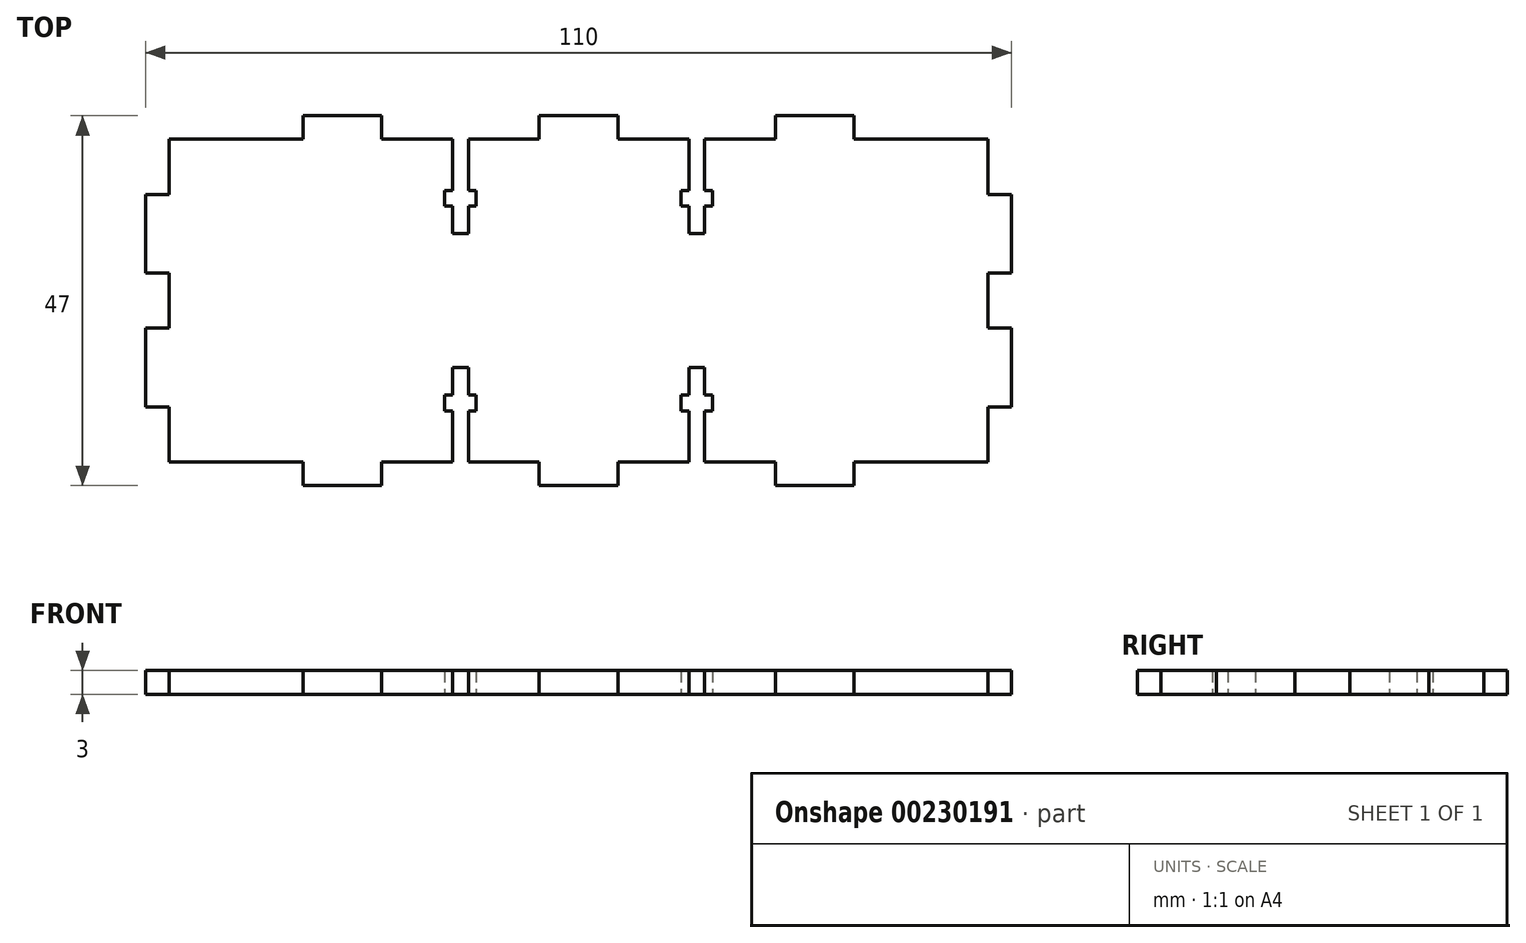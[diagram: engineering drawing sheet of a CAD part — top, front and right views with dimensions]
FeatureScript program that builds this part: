
annotation { "Feature Type Name" : "Feature", "Feature Type Description" : "" }
export const myFeature = defineFeature(function(context is Context, id is Id, definition is map)
    precondition{}
    {
        {
            var Q0;
            Q0=qCreatedBy(makeId("Top.planeOp"),FACE);
            var sketch = newSketch(context, id + "F0", { "sketchPlane" : qUnion([Q0])});
            skLineSegment(sketch, "E0", {"start": v(0, 0) * mm, "end": v(0, 7) * mm});
            skLineSegment(sketch, "E1", {"start": v(0, 7) * mm, "end": v(3, 7) * mm});
            skLineSegment(sketch, "E2", {"start": v(3, 7) * mm, "end": v(3, 17) * mm});
            skLineSegment(sketch, "E3", {"start": v(3, 17) * mm, "end": v(0, 17) * mm});
            skLineSegment(sketch, "E4", {"start": v(0, 17) * mm, "end": v(0, 24) * mm});
            skLineSegment(sketch, "E5", {"start": v(0, 24) * mm, "end": v(3, 24) * mm});
            skLineSegment(sketch, "E6", {"start": v(3, 24) * mm, "end": v(3, 34) * mm});
            skLineSegment(sketch, "E7", {"start": v(3, 34) * mm, "end": v(0, 34) * mm});
            skLineSegment(sketch, "E8", {"start": v(0, 34) * mm, "end": v(0, 41) * mm});
            skLineSegment(sketch, "E9", {"start": v(0, 41) * mm, "end": v(-17, 41) * mm});
            skLineSegment(sketch, "E10", {"start": v(-17, 41) * mm, "end": v(-17, 44) * mm});
            skLineSegment(sketch, "E11", {"start": v(-17, 44) * mm, "end": v(-27, 44) * mm});
            skLineSegment(sketch, "E12", {"start": v(-27, 44) * mm, "end": v(-27, 41) * mm});
            skLineSegment(sketch, "E13", {"start": v(-27, 41) * mm, "end": v(-36, 41) * mm});
            skLineSegment(sketch, "E14", {"start": v(-36, 41) * mm, "end": v(-36, 34.5) * mm});
            skLineSegment(sketch, "E15", {"start": v(-36, 34.5) * mm, "end": v(-35, 34.5) * mm});
            skLineSegment(sketch, "E16", {"start": v(-35, 34.5) * mm, "end": v(-35, 32.5) * mm});
            skLineSegment(sketch, "E17", {"start": v(-35, 32.5) * mm, "end": v(-36, 32.5) * mm});
            skLineSegment(sketch, "E18", {"start": v(-36, 32.5) * mm, "end": v(-36, 29) * mm});
            skLineSegment(sketch, "E19", {"start": v(-36, 29) * mm, "end": v(-38, 29) * mm});
            skLineSegment(sketch, "E20", {"start": v(-38, 29) * mm, "end": v(-38, 32.5) * mm});
            skLineSegment(sketch, "E21", {"start": v(-38, 32.5) * mm, "end": v(-39, 32.5) * mm});
            skLineSegment(sketch, "E22", {"start": v(-39, 32.5) * mm, "end": v(-39, 34.5) * mm});
            skLineSegment(sketch, "E23", {"start": v(-39, 34.5) * mm, "end": v(-38, 34.5) * mm});
            skLineSegment(sketch, "E24", {"start": v(-38, 34.5) * mm, "end": v(-38, 41) * mm});
            skLineSegment(sketch, "E25", {"start": v(-38, 41) * mm, "end": v(-47, 41) * mm});
            skLineSegment(sketch, "E26", {"start": v(-47, 41) * mm, "end": v(-47, 44) * mm});
            skLineSegment(sketch, "E27", {"start": v(-47, 44) * mm, "end": v(-52, 44) * mm});
            skLineSegment(sketch, "E28.MirrorCS", {"start": v(-39, 8.5) * mm, "end": v(-39, 6.5) * mm});
            skLineSegment(sketch, "E29.MirrorCS", {"start": v(-35, 6.5) * mm, "end": v(-35, 8.5) * mm});
            skLineSegment(sketch, "E30.MirrorCS", {"start": v(-38, 8.5) * mm, "end": v(-39, 8.5) * mm});
            skLineSegment(sketch, "E31.MirrorCS", {"start": v(-39, 6.5) * mm, "end": v(-38, 6.5) * mm});
            skLineSegment(sketch, "E32.MirrorCS", {"start": v(-36, 12) * mm, "end": v(-38, 12) * mm});
            skLineSegment(sketch, "E33.MirrorCS", {"start": v(-35, 8.5) * mm, "end": v(-36, 8.5) * mm});
            skLineSegment(sketch, "E34.MirrorCS", {"start": v(-36, 6.5) * mm, "end": v(-35, 6.5) * mm});
            skLineSegment(sketch, "E35.MirrorCS", {"start": v(-36, 8.5) * mm, "end": v(-36, 12) * mm});
            skLineSegment(sketch, "E36.MirrorCS", {"start": v(-38, 12) * mm, "end": v(-38, 8.5) * mm});
            skLineSegment(sketch, "E37.MirrorCS", {"start": v(0, 17) * mm, "end": v(3, 17) * mm});
            skLineSegment(sketch, "E38.MirrorCS", {"start": v(-47, 0) * mm, "end": v(-47, -3) * mm});
            skLineSegment(sketch, "E39.MirrorCS", {"start": v(3, 17) * mm, "end": v(3, 7) * mm});
            skLineSegment(sketch, "E40.MirrorCS", {"start": v(0, 7) * mm, "end": v(0, 0) * mm});
            skLineSegment(sketch, "E41.MirrorCS", {"start": v(3, 7) * mm, "end": v(0, 7) * mm});
            skLineSegment(sketch, "E42.MirrorCS", {"start": v(-38, 0) * mm, "end": v(-47, 0) * mm});
            skLineSegment(sketch, "E43.MirrorCS", {"start": v(-47, -3) * mm, "end": v(-52, -3) * mm});
            skLineSegment(sketch, "E44.MirrorCS", {"start": v(-27, -3) * mm, "end": v(-27, 0) * mm});
            skLineSegment(sketch, "E45.MirrorCS", {"start": v(0, 0) * mm, "end": v(-17, 0) * mm});
            skLineSegment(sketch, "E46.MirrorCS", {"start": v(-38, 6.5) * mm, "end": v(-38, 0) * mm});
            skLineSegment(sketch, "E47.MirrorCS", {"start": v(-27, 0) * mm, "end": v(-36, 0) * mm});
            skLineSegment(sketch, "E48.MirrorCS", {"start": v(-17, 0) * mm, "end": v(-17, -3) * mm});
            skLineSegment(sketch, "E49.MirrorCS", {"start": v(-17, -3) * mm, "end": v(-27, -3) * mm});
            skLineSegment(sketch, "E50.MirrorCS", {"start": v(-36, 0) * mm, "end": v(-36, 6.5) * mm});
            skLineSegment(sketch, "E51.MirrorCS", {"start": v(-107, 7) * mm, "end": v(-104, 7) * mm});
            skLineSegment(sketch, "E52.MirrorCS", {"start": v(-69, 32.5) * mm, "end": v(-68, 32.5) * mm});
            skLineSegment(sketch, "E53.MirrorCS", {"start": v(-104, 7) * mm, "end": v(-107, 7) * mm});
            skLineSegment(sketch, "E54.MirrorCS", {"start": v(-107, 17) * mm, "end": v(-104, 17) * mm});
            skLineSegment(sketch, "E55.MirrorCS", {"start": v(-69, 34.5) * mm, "end": v(-69, 32.5) * mm});
            skLineSegment(sketch, "E56.MirrorCS", {"start": v(-66, 8.5) * mm, "end": v(-65, 8.5) * mm});
            skLineSegment(sketch, "E57.MirrorCS", {"start": v(-104, 17) * mm, "end": v(-107, 17) * mm});
            skLineSegment(sketch, "E58.MirrorCS", {"start": v(-65, 32.5) * mm, "end": v(-65, 34.5) * mm});
            skLineSegment(sketch, "E59.MirrorCS", {"start": v(-69, 6.5) * mm, "end": v(-69, 8.5) * mm});
            skLineSegment(sketch, "E60.MirrorCS", {"start": v(-66, 32.5) * mm, "end": v(-65, 32.5) * mm});
            skLineSegment(sketch, "E61.MirrorCS", {"start": v(-68, 34.5) * mm, "end": v(-69, 34.5) * mm});
            skLineSegment(sketch, "E62.MirrorCS", {"start": v(-68, 6.5) * mm, "end": v(-69, 6.5) * mm});
            skLineSegment(sketch, "E63.MirrorCS", {"start": v(-65, 8.5) * mm, "end": v(-65, 6.5) * mm});
            skLineSegment(sketch, "E64.MirrorCS", {"start": v(-68, 32.5) * mm, "end": v(-68, 29) * mm});
            skLineSegment(sketch, "E65.MirrorCS", {"start": v(-68, 12) * mm, "end": v(-66, 12) * mm});
            skLineSegment(sketch, "E66.MirrorCS", {"start": v(-87, 0) * mm, "end": v(-87, -3) * mm});
            skLineSegment(sketch, "E67.MirrorCS", {"start": v(-69, 8.5) * mm, "end": v(-68, 8.5) * mm});
            skLineSegment(sketch, "E68.MirrorCS", {"start": v(-66, 12) * mm, "end": v(-66, 8.5) * mm});
            skLineSegment(sketch, "E69.MirrorCS", {"start": v(-65, 6.5) * mm, "end": v(-66, 6.5) * mm});
            skLineSegment(sketch, "E70.MirrorCS", {"start": v(-87, 41) * mm, "end": v(-87, 44) * mm});
            skLineSegment(sketch, "E71.MirrorCS", {"start": v(-107, 34) * mm, "end": v(-104, 34) * mm});
            skLineSegment(sketch, "E72.MirrorCS", {"start": v(-57, 0) * mm, "end": v(-57, -3) * mm});
            skLineSegment(sketch, "E73.MirrorCS", {"start": v(-77, 44) * mm, "end": v(-77, 41) * mm});
            skLineSegment(sketch, "E74.MirrorCS", {"start": v(-66, 29) * mm, "end": v(-66, 32.5) * mm});
            skLineSegment(sketch, "E75.MirrorCS", {"start": v(-57, 41) * mm, "end": v(-57, 44) * mm});
            skLineSegment(sketch, "E76.MirrorCS", {"start": v(-65, 34.5) * mm, "end": v(-66, 34.5) * mm});
            skLineSegment(sketch, "E77.MirrorCS", {"start": v(-104, 24) * mm, "end": v(-107, 24) * mm});
            skLineSegment(sketch, "E78.MirrorCS", {"start": v(-68, 29) * mm, "end": v(-66, 29) * mm});
            skLineSegment(sketch, "E79.MirrorCS", {"start": v(-77, -3) * mm, "end": v(-77, 0) * mm});
            skLineSegment(sketch, "E80.MirrorCS", {"start": v(-68, 8.5) * mm, "end": v(-68, 12) * mm});
            skLineSegment(sketch, "E81.MirrorCS", {"start": v(-104, 0) * mm, "end": v(-104, 7) * mm});
            skLineSegment(sketch, "E82.MirrorCS", {"start": v(-107, 7) * mm, "end": v(-107, 17) * mm});
            skLineSegment(sketch, "E83.MirrorCS", {"start": v(-57, 44) * mm, "end": v(-52, 44) * mm});
            skLineSegment(sketch, "E84.MirrorCS", {"start": v(-87, -3) * mm, "end": v(-77, -3) * mm});
            skLineSegment(sketch, "E85.MirrorCS", {"start": v(-66, 6.5) * mm, "end": v(-66, 0) * mm});
            skLineSegment(sketch, "E86.MirrorCS", {"start": v(-66, 41) * mm, "end": v(-57, 41) * mm});
            skLineSegment(sketch, "E87.MirrorCS", {"start": v(-104, 7) * mm, "end": v(-104, 0) * mm});
            skLineSegment(sketch, "E88.MirrorCS", {"start": v(-104, 0) * mm, "end": v(-87, 0) * mm});
            skLineSegment(sketch, "E89.MirrorCS", {"start": v(-66, 34.5) * mm, "end": v(-66, 41) * mm});
            skLineSegment(sketch, "E90.MirrorCS", {"start": v(-107, 17) * mm, "end": v(-107, 7) * mm});
            skLineSegment(sketch, "E91.MirrorCS", {"start": v(-57, -3) * mm, "end": v(-52, -3) * mm});
            skLineSegment(sketch, "E92.MirrorCS", {"start": v(-104, 41) * mm, "end": v(-87, 41) * mm});
            skLineSegment(sketch, "E93.MirrorCS", {"start": v(-87, 44) * mm, "end": v(-77, 44) * mm});
            skLineSegment(sketch, "E94.MirrorCS", {"start": v(-77, 0) * mm, "end": v(-68, 0) * mm});
            skLineSegment(sketch, "E95.MirrorCS", {"start": v(-104, 34) * mm, "end": v(-104, 41) * mm});
            skLineSegment(sketch, "E96.MirrorCS", {"start": v(-107, 24) * mm, "end": v(-107, 34) * mm});
            skLineSegment(sketch, "E97.MirrorCS", {"start": v(-66, 0) * mm, "end": v(-57, 0) * mm});
            skLineSegment(sketch, "E98.MirrorCS", {"start": v(-104, 17) * mm, "end": v(-104, 24) * mm});
            skLineSegment(sketch, "E99.MirrorCS", {"start": v(-68, 41) * mm, "end": v(-68, 34.5) * mm});
            skLineSegment(sketch, "E100.MirrorCS", {"start": v(-77, 41) * mm, "end": v(-68, 41) * mm});
            skLineSegment(sketch, "E101.MirrorCS", {"start": v(-68, 0) * mm, "end": v(-68, 6.5) * mm});
            skSolve(sketch);
        }
        {
            var Q0;
            Q0=makeQuery(id+"F0.imprint","IMPRINT",FACE,{"disambiguationData":[TD([[makeQuery(id+"F0.imprint","IMPRINT",EDGE,{"derivedFrom":sQuery(id+"F0.wireOp",EDGE,"E4")}),1.0]])]});
            extrude(context, id + "F1", {"entities" : qUnion([Q0]), "depth" : 3 * mm});
        }
    });
